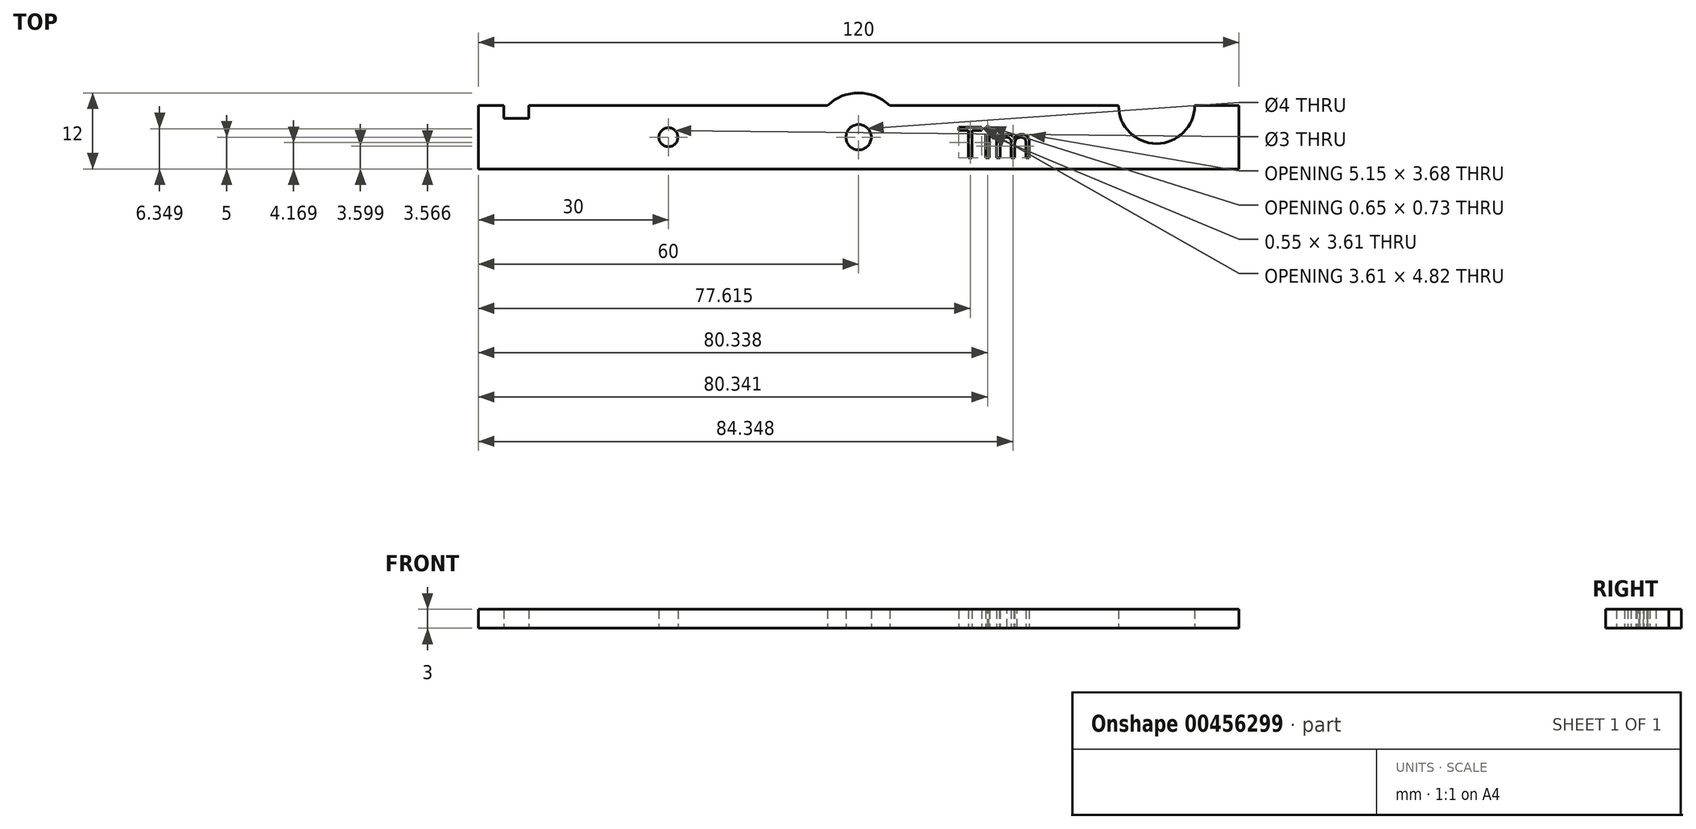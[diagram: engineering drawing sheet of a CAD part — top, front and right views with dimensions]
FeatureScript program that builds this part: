
annotation { "Feature Type Name" : "Feature", "Feature Type Description" : "" }
export const myFeature = defineFeature(function(context is Context, id is Id, definition is map)
    precondition{}
    {
        {
            var Q0;
            Q0=qCreatedBy(makeId("Top.planeOp"),FACE);
            var sketch = newSketch(context, id + "F0", { "sketchPlane" : qUnion([Q0])});
            skLineSegment(sketch, "E0.bottom", {"start": v(-60, -5) * mm, "end": v(60, -5) * mm});
            skLineSegment(sketch, "E0.top", {"start": v(-60, 5) * mm, "end": v(60, 5) * mm});
            skLineSegment(sketch, "E0.left", {"start": v(-60, -5) * mm, "end": v(-60, 5) * mm});
            skLineSegment(sketch, "E0.right", {"start": v(60, -5) * mm, "end": v(60, 5) * mm});
            skPoint(sketch, "E0.middle", {"position": v(0, 0) * mm});
            skLineSegment(sketch, "E1.bottom", {"start": v(-52, 3) * mm, "end": v(-56, 3) * mm});
            skLineSegment(sketch, "E1.top", {"start": v(-52, 5) * mm, "end": v(-56, 5) * mm});
            skLineSegment(sketch, "E1.left", {"start": v(-52, 3) * mm, "end": v(-52, 5) * mm});
            skLineSegment(sketch, "E1.right", {"start": v(-56, 3) * mm, "end": v(-56, 5) * mm});
            skPoint(sketch, "E1.middle", {"position": v(-54, 4) * mm});
            skCircle(sketch, "E2", {"center": v(0, 0) * mm, "radius": 2 * mm});
            skCircle(sketch, "E3", {"center": v(0, 0) * mm, "radius": 7 * mm});
            skCircle(sketch, "E4", {"center": v(-30, 0) * mm, "radius": 1.5 * mm});
            skCircle(sketch, "E5", {"center": v(47, 5) * mm, "radius": 6 * mm});
            skText(sketch, "E6", { "text": "Tim\n", "fontName": "OpenSans-Regular.ttf"});
            const initialGuessF0  = {"E6": [0.01575, -0.00324, 1, 0, 0.00486]};
            skSetInitialGuess(sketch, initialGuessF0);
            skSolve(sketch);
        }
        {
            var Q0;
            {var subQ0=sQuery(id+"F0.wireOp",EDGE,"E3");var subQ1=sQuery(id+"F0.wireOp",EDGE,"E0.bottom");var subQ2=makeQuery(id+"F0.imprint","INTERSECT",VERTEX,{"disambiguationData":[OD(0.0)],"derivedFrom":[subQ1,subQ0]});Q0=makeQuery(id+"F0.imprint","IMPRINT",FACE,{"disambiguationData":[TD([[makeQuery(id+"F0.imprint","IMPRINT",EDGE,{"disambiguationData":[TD([[subQ2,-1.0]])],"derivedFrom":subQ1}),-1.0]])]});}
            var Q1;
            {var subQ0=sQuery(id+"F0.wireOp",EDGE,"E3");var subQ1=sQuery(id+"F0.wireOp",EDGE,"E0.top");var subQ2=makeQuery(id+"F0.imprint","INTERSECT",VERTEX,{"disambiguationData":[OD(0.0)],"derivedFrom":[subQ1,subQ0]});Q1=makeQuery(id+"F0.imprint","IMPRINT",FACE,{"disambiguationData":[TD([[makeQuery(id+"F0.imprint","IMPRINT",EDGE,{"disambiguationData":[TD([[subQ2,-1.0]])],"derivedFrom":subQ1}),1.0]])]});}
            var Q2;
            {var subQ0=sQuery(id+"F0.wireOp",EDGE,"E0.left");Q2=makeQuery(id+"F0.imprint","IMPRINT",FACE,{"disambiguationData":[TD([[makeQuery(id+"F0.imprint","IMPRINT",EDGE,{"derivedFrom":subQ0}),-1.0]])]});}
            var Q3;
            Q3=makeQuery(id+"F0.imprint","IMPRINT",FACE,{"disambiguationData":[TD([[makeQuery(id+"F0.imprint","IMPRINT",EDGE,{"derivedFrom":sQuery(id+"F0.wireOp",EDGE,"E2")}),-1.0]])]});
            var Q4;
            {var subQ0=sQuery(id+"F0.wireOp",EDGE,"E0.right");Q4=makeQuery(id+"F0.imprint","IMPRINT",FACE,{"disambiguationData":[TD([[makeQuery(id+"F0.imprint","IMPRINT",EDGE,{"derivedFrom":subQ0}),1.0]])]});}
            extrude(context, id + "F1", {"entities" : qUnion([Q0, Q1, Q2, Q3, Q4]), "depth" : 3 * mm});
        }
    });
